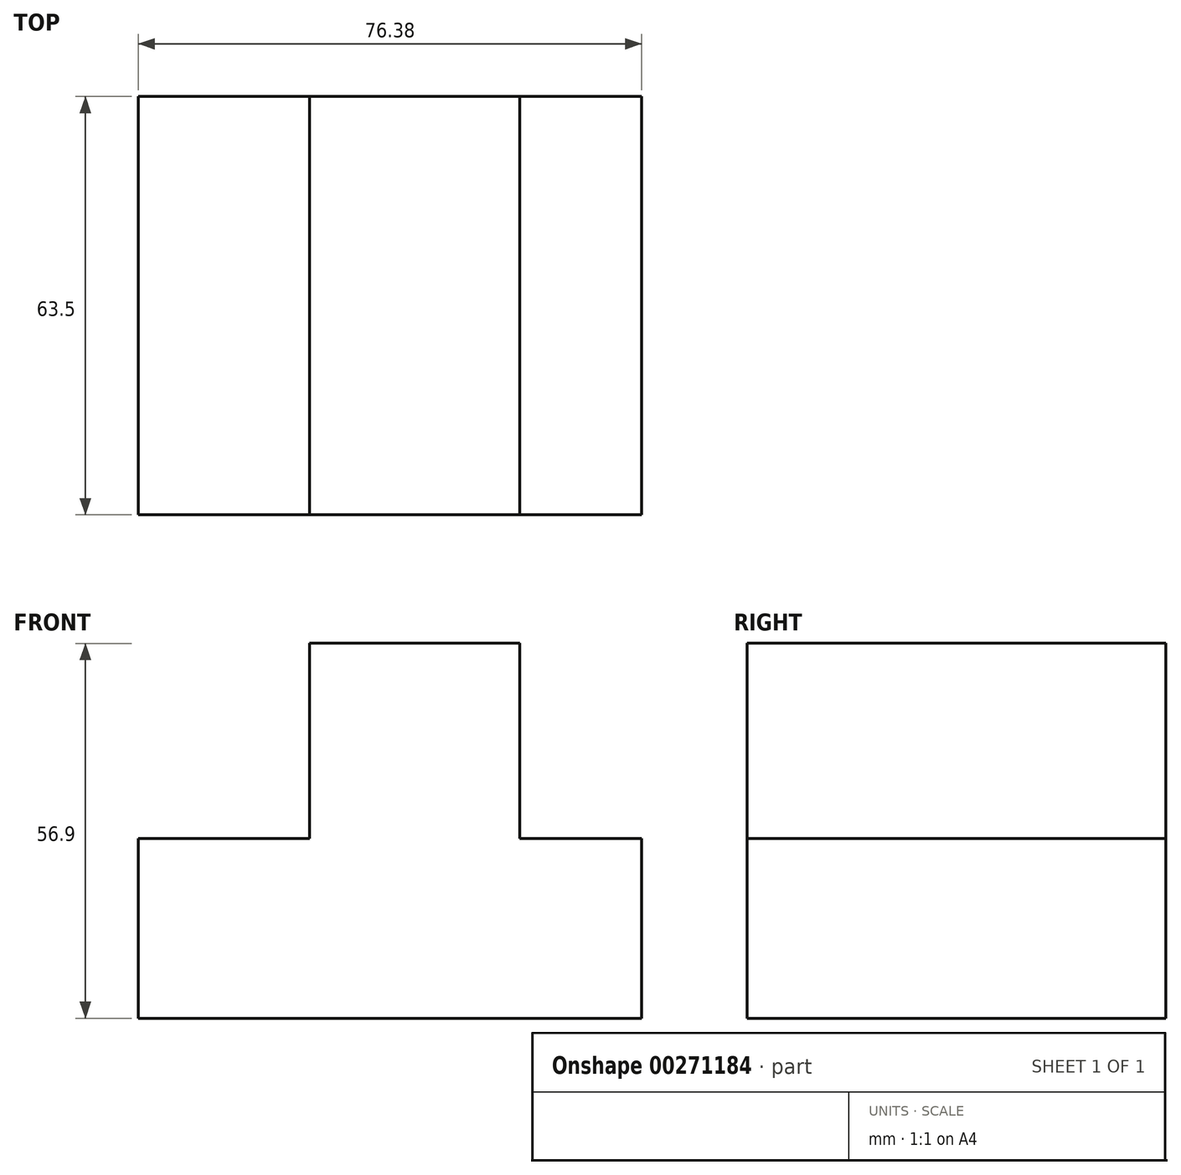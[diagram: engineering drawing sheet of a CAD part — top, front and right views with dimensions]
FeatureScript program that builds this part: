
annotation { "Feature Type Name" : "Feature", "Feature Type Description" : "" }
export const myFeature = defineFeature(function(context is Context, id is Id, definition is map)
    precondition{}
    {
        {
            var Q0;
            Q0=qCreatedBy(makeId("Front.planeOp"),FACE);
            var sketch = newSketch(context, id + "F0", { "sketchPlane" : qUnion([Q0])});
            skLineSegment(sketch, "E0.bottom", {"start": v(0, 0) * mm, "end": v(-76.38, 0) * mm});
            skLineSegment(sketch, "E0.top", {"start": v(0, 27.3) * mm, "end": v(-76.38, 27.3) * mm});
            skLineSegment(sketch, "E0.left", {"start": v(0, 0) * mm, "end": v(0, 27.3) * mm});
            skLineSegment(sketch, "E0.right", {"start": v(-76.38, 0) * mm, "end": v(-76.38, 27.3) * mm});
            skLineSegment(sketch, "E1.bottom", {"start": v(-18.52, 27.3) * mm, "end": v(-50.41, 27.3) * mm});
            skLineSegment(sketch, "E1.top", {"start": v(-18.52, 56.9) * mm, "end": v(-50.41, 56.9) * mm});
            skLineSegment(sketch, "E1.left", {"start": v(-18.52, 27.3) * mm, "end": v(-18.52, 56.9) * mm});
            skLineSegment(sketch, "E1.right", {"start": v(-50.41, 27.3) * mm, "end": v(-50.41, 56.9) * mm});
            skSolve(sketch);
        }
        {
            var Q0;
            Q0 = qSketchRegion(id + "F0", true);
            extrude(context, id + "F1", {"entities" : qUnion([Q0]), "depth" : 63.5 * mm});
        }
    });
